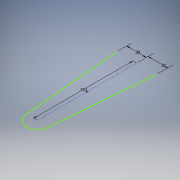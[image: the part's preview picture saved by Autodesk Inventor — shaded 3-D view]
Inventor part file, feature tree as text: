
AUTODESK INVENTOR PART (.ipt)
format: ipt  version: 2018 (Build 220112000, 112)  size: 87,552 bytes
history: native  units: mm
features: sketch x1
ambient origin geometry x8: Origin, YZ Plane, XZ Plane, XY Plane, X Axis, Y Axis, Z Axis, Center Point
feature tree (1):
  sketch  "Sketch1"  dims[d0=150.0mm d2=30.0mm d3=30.0mm]
